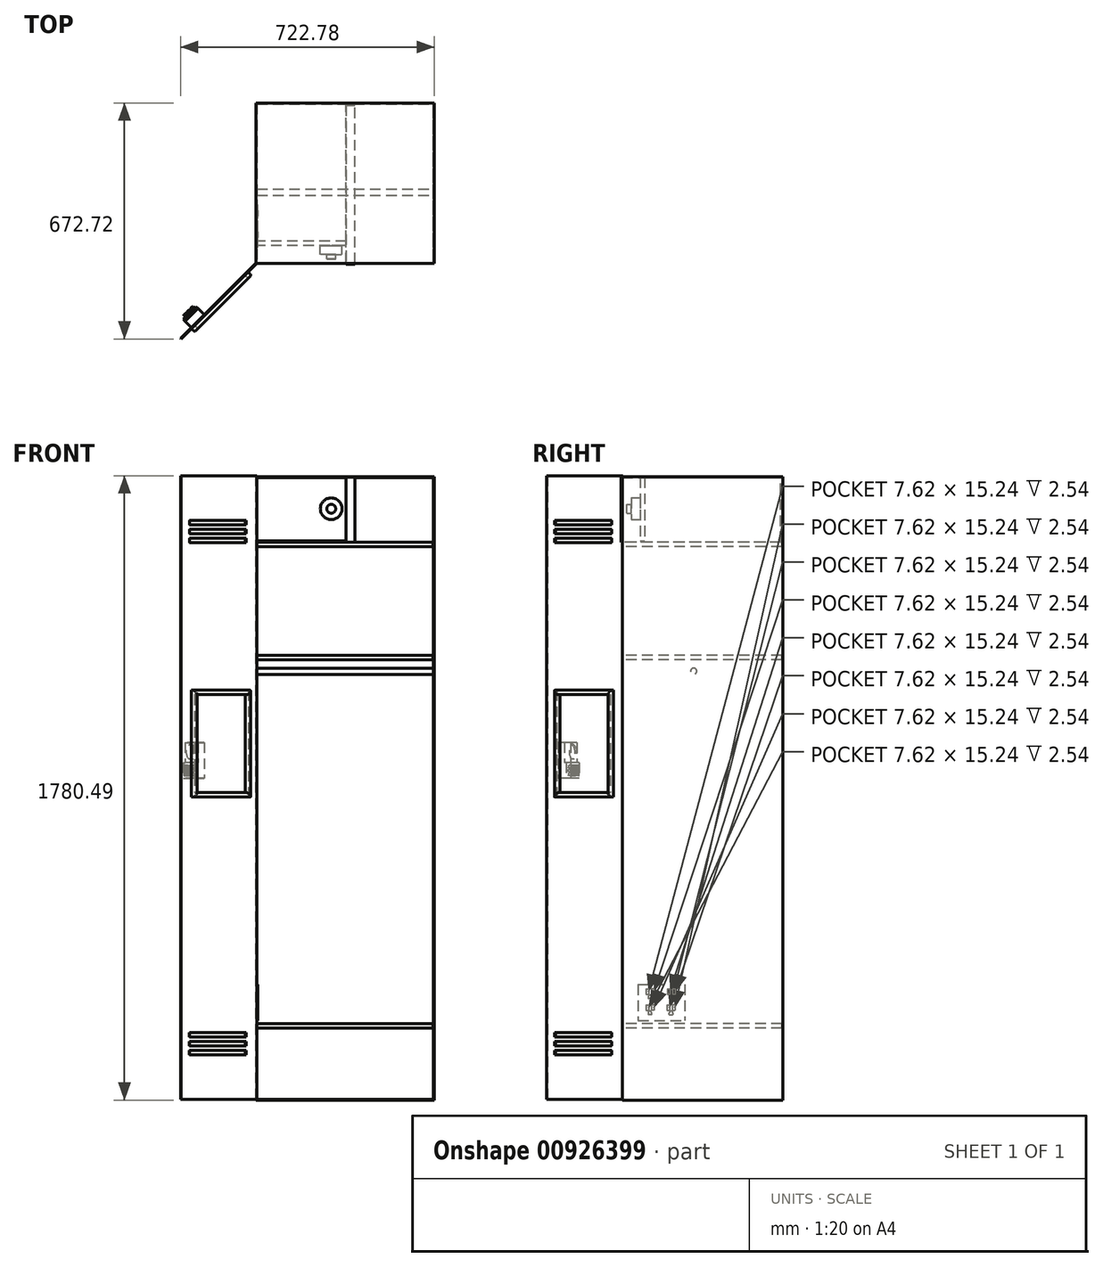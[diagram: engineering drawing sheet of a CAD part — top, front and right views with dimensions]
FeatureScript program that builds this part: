
annotation { "Feature Type Name" : "Feature", "Feature Type Description" : "" }
export const myFeature = defineFeature(function(context is Context, id is Id, definition is map)
    precondition{}
    {
        {
            var Q0;
            Q0=qCreatedBy(makeId("Front.planeOp"),FACE);
            var sketch = newSketch(context, id + "F0", { "sketchPlane" : qUnion([Q0])});
            skLineSegment(sketch, "E0.bottom", {"start": v(-28.78, 1709) * mm, "end": v(479.22, 1709) * mm});
            skLineSegment(sketch, "E0.top", {"start": v(-28.78, -69) * mm, "end": v(479.22, -69) * mm});
            skLineSegment(sketch, "E0.left", {"start": v(-28.78, 1709) * mm, "end": v(-28.78, -69) * mm});
            skLineSegment(sketch, "E0.right", {"start": v(479.22, 1709) * mm, "end": v(479.22, -69) * mm});
            skPoint(sketch, "E1", {"position": v(-28.78, 1709) * mm});
            skPoint(sketch, "E2", {"position": v(-28.78, -69) * mm});
            skSolve(sketch);
        }
        {
            var Q0;
            Q0 = qSketchRegion(id + "F0", true);
            extrude(context, id + "F1", {"entities" : qUnion([Q0]), "depth" : 457.2 * mm, "offsetDistance" : 25.4 * mm});
        }
        {
            var Q0;
            Q0=makeQuery(id+"F1.opExtrude","CAP_FACE",FACE,{"disambiguationData":[OSD([sQuery(id+"F0.wireOp",EDGE,"E0.bottom"),sQuery(id+"F0.wireOp",EDGE,"E0.top"),sQuery(id+"F0.wireOp",EDGE,"E0.left"),sQuery(id+"F0.wireOp",EDGE,"E0.right")])],"isStart":false});
            shell(context, id + "F2", {"entities" : qUnion([Q0]), "thickness" : 2.54 * mm});
        }
        {
            var Q0;
            {var subQ0=sQuery(id+"F0.wireOp",EDGE,"E0.left");Q0=makeQuery(id+"F2.opShell","OFFSET_EDGE",EDGE,{"disambiguationData":[OSD([subQ0]),TDD([makeQuery(id+"F1.opExtrude","CAP_EDGE",EDGE,{"disambiguationData":[OSD([subQ0])],"isStart":false})])]});}
            cPlane(context, id + "F3", {"entities" : qUnion([Q0]), "cplaneType" : CPlaneType.LINE_ANGLE, "offset" : 25.4 * mm, "angle" : 45 * degree, "width" : 152.4 * mm, "height" : 152.4 * mm});
        }
        {
            var Q0;
            Q0=makeQuery(id+"F2.opShell","OFFSET_FACE",FACE,{"disambiguationData":[OSD([sQuery(id+"F0.wireOp",EDGE,"E0.left")])]});
            var sketch = newSketch(context, id + "F4", { "sketchPlane" : qUnion([Q0])});
            skPoint(sketch, "E3", {"position": v(-457.2, 1706.45) * mm});
            skPoint(sketch, "E4", {"position": v(-457.2, -66.47) * mm});
            skSolve(sketch);
        }
        {
            var Q0;
            Q0=qCreatedBy(id+"F3.planeOp",FACE);
            var sketch = newSketch(context, id + "F5", { "sketchPlane" : qUnion([Q0])});
            skLineSegment(sketch, "E5.bottom", {"start": v(341.83, 1711.48) * mm, "end": v(646.63, 1711.48) * mm});
            skLineSegment(sketch, "E5.top", {"start": v(341.83, -66.52) * mm, "end": v(646.63, -66.52) * mm});
            skLineSegment(sketch, "E5.left", {"start": v(341.83, 1711.48) * mm, "end": v(341.83, -66.52) * mm});
            skLineSegment(sketch, "E5.right", {"start": v(646.63, 1711.48) * mm, "end": v(646.63, -66.52) * mm});
            skLineSegment(sketch, "E6.bottom", {"start": v(385.44, 1584.48) * mm, "end": v(614.04, 1584.48) * mm});
            skLineSegment(sketch, "E6.top", {"start": v(385.44, 1571.78) * mm, "end": v(614.04, 1571.78) * mm});
            skLineSegment(sketch, "E6.left", {"start": v(385.44, 1584.48) * mm, "end": v(385.44, 1571.78) * mm});
            skLineSegment(sketch, "E6.right", {"start": v(614.04, 1584.48) * mm, "end": v(614.04, 1571.78) * mm});
            skLineSegment(sketch, "E7.bottom", {"start": v(614.04, 1559.08) * mm, "end": v(385.44, 1559.08) * mm});
            skLineSegment(sketch, "E7.top", {"start": v(614.04, 1546.38) * mm, "end": v(385.44, 1546.38) * mm});
            skLineSegment(sketch, "E7.left", {"start": v(614.04, 1559.08) * mm, "end": v(614.04, 1546.38) * mm});
            skLineSegment(sketch, "E7.right", {"start": v(385.44, 1559.08) * mm, "end": v(385.44, 1546.38) * mm});
            skLineSegment(sketch, "E8.bottom", {"start": v(614.04, 1533.68) * mm, "end": v(385.44, 1533.68) * mm});
            skLineSegment(sketch, "E8.top", {"start": v(614.04, 1520.98) * mm, "end": v(385.44, 1520.98) * mm});
            skLineSegment(sketch, "E8.left", {"start": v(614.04, 1533.68) * mm, "end": v(614.04, 1520.98) * mm});
            skLineSegment(sketch, "E8.right", {"start": v(385.44, 1533.68) * mm, "end": v(385.44, 1520.98) * mm});
            skLineSegment(sketch, "E9", {"start": v(579.57, -66.52) * mm, "end": v(579.57, 822.48) * mm, "construction": true});
            skLineSegment(sketch, "E10", {"start": v(646.63, 822.48) * mm, "end": v(341.83, 822.48) * mm, "construction": true});
            skLineSegment(sketch, "E11.MirrorCS", {"start": v(614.04, 123.98) * mm, "end": v(385.44, 123.98) * mm});
            skLineSegment(sketch, "E12.MirrorCS", {"start": v(614.04, 111.28) * mm, "end": v(385.44, 111.28) * mm});
            skLineSegment(sketch, "E13.MirrorCS", {"start": v(614.04, 98.58) * mm, "end": v(385.44, 98.58) * mm});
            skLineSegment(sketch, "E14.MirrorCS", {"start": v(614.04, 85.88) * mm, "end": v(385.44, 85.88) * mm});
            skLineSegment(sketch, "E15.MirrorCS", {"start": v(385.44, 73.18) * mm, "end": v(614.04, 73.18) * mm});
            skLineSegment(sketch, "E16.MirrorCS", {"start": v(385.44, 60.48) * mm, "end": v(614.04, 60.48) * mm});
            skLineSegment(sketch, "E17.MirrorCS", {"start": v(385.44, 60.48) * mm, "end": v(385.44, 73.18) * mm});
            skLineSegment(sketch, "E18.MirrorCS", {"start": v(385.44, 85.88) * mm, "end": v(385.44, 98.58) * mm});
            skLineSegment(sketch, "E19.MirrorCS", {"start": v(385.44, 111.28) * mm, "end": v(385.44, 123.98) * mm});
            skLineSegment(sketch, "E20.MirrorCS", {"start": v(614.04, 111.28) * mm, "end": v(614.04, 123.98) * mm});
            skLineSegment(sketch, "E21.MirrorCS", {"start": v(614.04, 85.88) * mm, "end": v(614.04, 98.58) * mm});
            skLineSegment(sketch, "E22.MirrorCS", {"start": v(614.04, 60.48) * mm, "end": v(614.04, 73.18) * mm});
            skSolve(sketch);
        }
        {
            var Q0;
            Q0=makeQuery(id+"F5.imprint","IMPRINT",FACE,{"disambiguationData":[TD([[makeQuery(id+"F5.imprint","IMPRINT",EDGE,{"derivedFrom":sQuery(id+"F5.wireOp",EDGE,"E5.bottom")}),-1.0]])]});
            extrude(context, id + "F6", {"entities" : qUnion([Q0]), "operationType" : NewBodyOperationType.ADD, "depth" : 2.54 * mm, "offsetDistance" : 25.4 * mm});
        }
        {
            var Q0;
            Q0=makeQuery(id+"F6.opExtrude","CAP_FACE",FACE,{"disambiguationData":[OSD([sQuery(id+"F5.wireOp",EDGE,"E5.bottom"),sQuery(id+"F5.wireOp",EDGE,"E5.top"),sQuery(id+"F5.wireOp",EDGE,"E5.left"),sQuery(id+"F5.wireOp",EDGE,"E5.right"),sQuery(id+"F5.wireOp",EDGE,"E6.bottom"),sQuery(id+"F5.wireOp",EDGE,"E6.top"),sQuery(id+"F5.wireOp",EDGE,"E6.left"),sQuery(id+"F5.wireOp",EDGE,"E6.right"),sQuery(id+"F5.wireOp",EDGE,"E7.bottom"),sQuery(id+"F5.wireOp",EDGE,"E7.top"),sQuery(id+"F5.wireOp",EDGE,"E7.left"),sQuery(id+"F5.wireOp",EDGE,"E7.right"),sQuery(id+"F5.wireOp",EDGE,"E8.bottom"),sQuery(id+"F5.wireOp",EDGE,"E8.top"),sQuery(id+"F5.wireOp",EDGE,"E8.left"),sQuery(id+"F5.wireOp",EDGE,"E8.right")])],"isStart":false});
            var sketch = newSketch(context, id + "F7", { "sketchPlane" : qUnion([Q0])});
            skLineSegment(sketch, "E23.bottom", {"start": v(551.95, 950.81) * mm, "end": v(602.75, 950.81) * mm});
            skLineSegment(sketch, "E23.top", {"start": v(551.95, 849.21) * mm, "end": v(602.75, 849.21) * mm});
            skLineSegment(sketch, "E23.left", {"start": v(551.95, 950.81) * mm, "end": v(551.95, 849.21) * mm});
            skLineSegment(sketch, "E23.right", {"start": v(602.75, 950.81) * mm, "end": v(602.75, 849.21) * mm});
            skSolve(sketch);
        }
        {
            var Q0;
            Q0=makeQuery(id+"F7.imprint","IMPRINT",FACE,{"disambiguationData":[TD([[makeQuery(id+"F7.imprint","IMPRINT",EDGE,{"derivedFrom":sQuery(id+"F7.wireOp",EDGE,"E23.bottom")}),-1.0]])]});
            extrude(context, id + "F8", {"entities" : qUnion([Q0]), "operationType" : NewBodyOperationType.ADD, "depth" : 25.4 * mm, "offsetDistance" : 25.4 * mm});
        }
        {
            var Q0;
            Q0=qCreatedBy(makeId("Front.planeOp"),FACE);
            cPlane(context, id + "F9", {"entities" : qUnion([Q0]), "cplaneType" : CPlaneType.OFFSET, "offset" : 457.2 * mm, "width" : 152.4 * mm, "height" : 152.4 * mm});
        }
        {
            var Q0;
            Q0=qCreatedBy(id+"F9.planeOp",FACE);
            var sketch = newSketch(context, id + "F10", { "sketchPlane" : qUnion([Q0])});
            skLineSegment(sketch, "E24.bottom", {"start": v(-26.2, 149.43) * mm, "end": v(474.94, 149.43) * mm});
            skLineSegment(sketch, "E24.top", {"start": v(-26.2, 136.73) * mm, "end": v(474.94, 136.73) * mm});
            skLineSegment(sketch, "E24.left", {"start": v(-26.2, 149.43) * mm, "end": v(-26.2, 136.73) * mm});
            skLineSegment(sketch, "E24.right", {"start": v(474.94, 149.43) * mm, "end": v(474.94, 136.73) * mm});
            skLineSegment(sketch, "E25.bottom", {"start": v(-26.6, 1199.69) * mm, "end": v(475.38, 1199.69) * mm});
            skLineSegment(sketch, "E25.top", {"start": v(-26.6, 1186.99) * mm, "end": v(475.38, 1186.99) * mm});
            skLineSegment(sketch, "E25.left", {"start": v(-26.6, 1199.69) * mm, "end": v(-26.6, 1186.99) * mm});
            skLineSegment(sketch, "E25.right", {"start": v(475.38, 1199.69) * mm, "end": v(475.38, 1186.99) * mm});
            skLineSegment(sketch, "E26.bottom", {"start": v(-25.76, 1522.03) * mm, "end": v(475.38, 1522.03) * mm});
            skLineSegment(sketch, "E26.top", {"start": v(-25.76, 1509.33) * mm, "end": v(475.38, 1509.33) * mm});
            skLineSegment(sketch, "E26.left", {"start": v(-25.76, 1522.03) * mm, "end": v(-25.76, 1509.33) * mm});
            skLineSegment(sketch, "E26.right", {"start": v(475.38, 1522.03) * mm, "end": v(475.38, 1509.33) * mm});
            skSolve(sketch);
        }
        {
            var Q0;
            Q0=makeQuery(id+"F10.imprint","IMPRINT",FACE,{"disambiguationData":[TD([[makeQuery(id+"F10.imprint","IMPRINT",EDGE,{"derivedFrom":sQuery(id+"F10.wireOp",EDGE,"E24.bottom")}),-1.0]])]});
            var Q1;
            Q1=makeQuery(id+"F10.imprint","IMPRINT",FACE,{"disambiguationData":[TD([[makeQuery(id+"F10.imprint","IMPRINT",EDGE,{"derivedFrom":sQuery(id+"F10.wireOp",EDGE,"VyrBGK2K-1y9x-VAEc-Igx1-qJqO2NATqdDI.bottom")}),-1.0]])]});
            var Q2;
            Q2=makeQuery(id+"F10.imprint","IMPRINT",FACE,{"disambiguationData":[TD([[makeQuery(id+"F10.imprint","IMPRINT",EDGE,{"derivedFrom":sQuery(id+"F10.wireOp",EDGE,"E25.bottom")}),-1.0]])]});
            var Q3;
            Q3=makeQuery(id+"F10.imprint","IMPRINT",FACE,{"disambiguationData":[TD([[makeQuery(id+"F10.imprint","IMPRINT",EDGE,{"derivedFrom":sQuery(id+"F10.wireOp",EDGE,"E26.bottom")}),-1.0]])]});
            extrude(context, id + "F11", {"entities" : qUnion([Q0, Q1, Q2, Q3]), "operationType" : NewBodyOperationType.ADD, "endBound" : BoundingType.UP_TO_NEXT, "oppositeDirection" : true, "depth" : 25.4 * mm, "offsetDistance" : 25.4 * mm});
        }
        {
            var Q0;
            {var subQ0=sQuery(id+"F10.wireOp",EDGE,"E24.bottom");var subQ1=sQuery(id+"F0.wireOp",EDGE,"E0.right");Q0=makeQuery(id+"F11.boolean.opBoolean","SPLIT",FACE,{"disambiguationData":[TD([makeQuery(id+"F11.opExtrude","SWEPT_FACE",FACE,{"disambiguationData":[OSD([subQ0])]})])],"derivedFrom":makeQuery(id+"F2.opShell","OFFSET_FACE",FACE,{"disambiguationData":[OSD([subQ1])]})});}
            var sketch = newSketch(context, id + "F12", { "sketchPlane" : qUnion([Q0])});
            skCircle(sketch, "E27", {"center": v(253.8, 1154.02) * mm, "radius": 8.9 * mm});
            skSolve(sketch);
        }
        {
            var Q0;
            Q0=makeQuery(id+"F12.imprint","IMPRINT",FACE,{"disambiguationData":[TD([[makeQuery(id+"F12.imprint","IMPRINT",EDGE,{"derivedFrom":sQuery(id+"F12.wireOp",EDGE,"E27")}),1.0]])]});
            extrude(context, id + "F13", {"entities" : qUnion([Q0]), "operationType" : NewBodyOperationType.ADD, "endBound" : BoundingType.UP_TO_NEXT, "depth" : 25.4 * mm, "offsetDistance" : 25.4 * mm});
        }
        {
            var Q0;
            Q0=makeQuery(id+"F6.opExtrude","CAP_FACE",FACE,{"disambiguationData":[OSD([sQuery(id+"F5.wireOp",EDGE,"E5.bottom"),sQuery(id+"F5.wireOp",EDGE,"E5.top"),sQuery(id+"F5.wireOp",EDGE,"E5.left"),sQuery(id+"F5.wireOp",EDGE,"E5.right"),sQuery(id+"F5.wireOp",EDGE,"E6.bottom"),sQuery(id+"F5.wireOp",EDGE,"E6.top"),sQuery(id+"F5.wireOp",EDGE,"E6.left"),sQuery(id+"F5.wireOp",EDGE,"E6.right"),sQuery(id+"F5.wireOp",EDGE,"E7.bottom"),sQuery(id+"F5.wireOp",EDGE,"E7.top"),sQuery(id+"F5.wireOp",EDGE,"E7.left"),sQuery(id+"F5.wireOp",EDGE,"E7.right"),sQuery(id+"F5.wireOp",EDGE,"E8.bottom"),sQuery(id+"F5.wireOp",EDGE,"E8.top"),sQuery(id+"F5.wireOp",EDGE,"E8.left"),sQuery(id+"F5.wireOp",EDGE,"E8.right"),sQuery(id+"F5.wireOp",EDGE,"E11.MirrorCS"),sQuery(id+"F5.wireOp",EDGE,"E12.MirrorCS"),sQuery(id+"F5.wireOp",EDGE,"E13.MirrorCS"),sQuery(id+"F5.wireOp",EDGE,"E14.MirrorCS"),sQuery(id+"F5.wireOp",EDGE,"E15.MirrorCS"),sQuery(id+"F5.wireOp",EDGE,"E16.MirrorCS"),sQuery(id+"F5.wireOp",EDGE,"E17.MirrorCS"),sQuery(id+"F5.wireOp",EDGE,"E18.MirrorCS"),sQuery(id+"F5.wireOp",EDGE,"E19.MirrorCS"),sQuery(id+"F5.wireOp",EDGE,"E20.MirrorCS"),sQuery(id+"F5.wireOp",EDGE,"E21.MirrorCS"),sQuery(id+"F5.wireOp",EDGE,"E22.MirrorCS")])],"isStart":true});
            var sketch = newSketch(context, id + "F14", { "sketchPlane" : qUnion([Q0])});
            skLineSegment(sketch, "E28.bottom", {"start": v(-605.48, 1099.56) * mm, "end": v(-376.88, 1099.56) * mm});
            skLineSegment(sketch, "E28.top", {"start": v(-605.48, 794.76) * mm, "end": v(-376.88, 794.76) * mm});
            skLineSegment(sketch, "E28.left", {"start": v(-605.48, 1099.56) * mm, "end": v(-605.48, 794.76) * mm});
            skLineSegment(sketch, "E28.right", {"start": v(-376.88, 1099.56) * mm, "end": v(-376.88, 794.76) * mm});
            skLineSegment(sketch, "E29.0", {"start": v(-592.78, 1086.86) * mm, "end": v(-389.58, 1086.86) * mm});
            skLineSegment(sketch, "E29.1", {"start": v(-592.78, 1086.86) * mm, "end": v(-592.78, 807.46) * mm});
            skLineSegment(sketch, "E29.2", {"start": v(-592.78, 807.46) * mm, "end": v(-389.58, 807.46) * mm});
            skLineSegment(sketch, "E29.3", {"start": v(-389.58, 1086.86) * mm, "end": v(-389.58, 807.46) * mm});
            skSolve(sketch);
        }
        {
            var Q0;
            Q0=makeQuery(id+"F14.imprint","IMPRINT",FACE,{"disambiguationData":[TD([[makeQuery(id+"F14.imprint","IMPRINT",EDGE,{"derivedFrom":sQuery(id+"F14.wireOp",EDGE,"E28.bottom")}),-1.0]])]});
            extrude(context, id + "F15", {"entities" : qUnion([Q0]), "operationType" : NewBodyOperationType.ADD, "depth" : 12.7 * mm, "offsetDistance" : 25.4 * mm});
        }
        {
            var Q0;
            Q0=makeQuery(id+"F15.opExtrude","CAP_EDGE",EDGE,{"disambiguationData":[OSD([sQuery(id+"F14.wireOp",EDGE,"E28.left")])],"isStart":false});
            var Q1;
            Q1=makeQuery(id+"F15.opExtrude","CAP_EDGE",EDGE,{"disambiguationData":[OSD([sQuery(id+"F14.wireOp",EDGE,"E28.bottom")])],"isStart":false});
            var Q2;
            Q2=makeQuery(id+"F15.opExtrude","CAP_EDGE",EDGE,{"disambiguationData":[OSD([sQuery(id+"F14.wireOp",EDGE,"E28.right")])],"isStart":false});
            var Q3;
            Q3=makeQuery(id+"F15.opExtrude","CAP_EDGE",EDGE,{"disambiguationData":[OSD([sQuery(id+"F14.wireOp",EDGE,"E28.top")])],"isStart":false});
            var Q4;
            Q4=makeQuery(id+"F15.opExtrude","CAP_EDGE",EDGE,{"disambiguationData":[OSD([sQuery(id+"F14.wireOp",EDGE,"E29.2")])],"isStart":false});
            var Q5;
            Q5=makeQuery(id+"F15.opExtrude","CAP_EDGE",EDGE,{"disambiguationData":[OSD([sQuery(id+"F14.wireOp",EDGE,"E29.3")])],"isStart":false});
            var Q6;
            Q6=makeQuery(id+"F15.opExtrude","CAP_EDGE",EDGE,{"disambiguationData":[OSD([sQuery(id+"F14.wireOp",EDGE,"E29.1")])],"isStart":false});
            var Q7;
            Q7=makeQuery(id+"F15.opExtrude","CAP_EDGE",EDGE,{"disambiguationData":[OSD([sQuery(id+"F14.wireOp",EDGE,"E29.0")])],"isStart":false});
            fillet(context, id + "F16", {"entities" : qUnion([Q0, Q1, Q2, Q3, Q4, Q5, Q6, Q7]), "radius" : 5.08 * mm, "tangentPropagation" : true, "allowEdgeOverflow" : false});
        }
        {
            var Q0;
            {var subQ0=sQuery(id+"F0.wireOp",EDGE,"E0.left");Q0=makeQuery(id+"F4.imprint","IMPRINT",FACE,{"disambiguationData":[TD([[makeQuery(id+"F4.imprint","IMPRINT",EDGE,{"derivedFrom":makeQuery(id+"F2.opShell","OFFSET_EDGE",EDGE,{"disambiguationData":[OSD([subQ0]),TDD([makeQuery(id+"F1.opExtrude","CAP_EDGE",EDGE,{"disambiguationData":[OSD([subQ0])],"isStart":true})])]})}),-1.0]])]});}
            var sketch = newSketch(context, id + "F17", { "sketchPlane" : qUnion([Q0])});
            skLineSegment(sketch, "E30.bottom", {"start": v(-406.4, 1707.77) * mm, "end": v(-393.7, 1707.77) * mm});
            skLineSegment(sketch, "E30.top", {"start": v(-406.4, 1525.9) * mm, "end": v(-393.7, 1525.9) * mm});
            skLineSegment(sketch, "E30.left", {"start": v(-406.4, 1707.77) * mm, "end": v(-406.4, 1525.9) * mm});
            skLineSegment(sketch, "E30.right", {"start": v(-393.7, 1707.77) * mm, "end": v(-393.7, 1525.9) * mm});
            skSolve(sketch);
        }
        {
            var Q0;
            {var subQ0=sQuery(id+"F17.wireOp",EDGE,"E30.top");Q0=makeQuery(id+"F17.imprint","IMPRINT",FACE,{"disambiguationData":[TD([[makeQuery(id+"F17.imprint","IMPRINT",EDGE,{"derivedFrom":subQ0}),1.0]])]});}
            extrude(context, id + "F18", {"entities" : qUnion([Q0]), "operationType" : NewBodyOperationType.ADD, "depth" : 254 * mm, "offsetDistance" : 25.4 * mm});
        }
        {
            var Q0;
            Q0=makeQuery(id+"F18.opExtrude","SWEPT_FACE",FACE,{"disambiguationData":[OSD([sQuery(id+"F17.wireOp",EDGE,"E30.left")])]});
            var sketch = newSketch(context, id + "F19", { "sketchPlane" : qUnion([Q0])});
            skCircle(sketch, "E31", {"center": v(185.47, 1617.22) * mm, "radius": 31.03 * mm});
            skSolve(sketch);
        }
        {
            var Q0;
            Q0=makeQuery(id+"F19.imprint","IMPRINT",FACE,{"disambiguationData":[TD([[makeQuery(id+"F19.imprint","IMPRINT",EDGE,{"derivedFrom":sQuery(id+"F19.wireOp",EDGE,"E31")}),1.0]])]});
            extrude(context, id + "F20", {"entities" : qUnion([Q0]), "operationType" : NewBodyOperationType.ADD, "depth" : 25.4 * mm, "offsetDistance" : 25.4 * mm});
        }
        {
            var Q0;
            Q0=makeQuery(id+"F20.opExtrude","CAP_FACE",FACE,{"disambiguationData":[OSD([sQuery(id+"F19.wireOp",EDGE,"E31")])],"isStart":false});
            var sketch = newSketch(context, id + "F21", { "sketchPlane" : qUnion([Q0])});
            skCircle(sketch, "E32", {"center": v(185.47, 1617.22) * mm, "radius": 12.7 * mm});
            skSolve(sketch);
        }
        {
            var Q0;
            Q0=makeQuery(id+"F21.imprint","IMPRINT",FACE,{"disambiguationData":[TD([[makeQuery(id+"F21.imprint","IMPRINT",EDGE,{"derivedFrom":sQuery(id+"F21.wireOp",EDGE,"E32")}),1.0]])]});
            extrude(context, id + "F22", {"entities" : qUnion([Q0]), "operationType" : NewBodyOperationType.ADD, "depth" : 12.7 * mm, "offsetDistance" : 25.4 * mm});
        }
        {
            var Q0;
            Q0=makeQuery(id+"F8.opExtrude","CAP_FACE",FACE,{"disambiguationData":[OSD([sQuery(id+"F7.wireOp",EDGE,"E23.bottom"),sQuery(id+"F7.wireOp",EDGE,"E23.top"),sQuery(id+"F7.wireOp",EDGE,"E23.left"),sQuery(id+"F7.wireOp",EDGE,"E23.right")])],"isStart":false});
            var sketch = newSketch(context, id + "F23", { "sketchPlane" : qUnion([Q0])});
            skEllipse(sketch, "E33", {"center": v(576.01, 923.91) * mm, "majorRadius": 21.07 * mm, "minorRadius": 13.97 * mm, "majorAxis": v(0, 1)});
            skLineSegment(sketch, "E34.bottom", {"start": v(551.95, 893.4) * mm, "end": v(602.75, 893.4) * mm});
            skLineSegment(sketch, "E34.top", {"start": v(551.95, 849.21) * mm, "end": v(602.75, 849.21) * mm});
            skLineSegment(sketch, "E34.left", {"start": v(551.95, 893.4) * mm, "end": v(551.95, 849.21) * mm});
            skLineSegment(sketch, "E34.right", {"start": v(602.75, 893.4) * mm, "end": v(602.75, 849.21) * mm});
            skSolve(sketch);
        }
        {
            var Q0;
            Q0=makeQuery(id+"F23.imprint","IMPRINT",FACE,{"disambiguationData":[TD([[makeQuery(id+"F23.imprint","IMPRINT",EDGE,{"derivedFrom":sQuery(id+"F23.wireOp",EDGE,"E33")}),1.0]])]});
            var Q1;
            Q1=makeQuery(id+"F23.imprint","IMPRINT",FACE,{"disambiguationData":[TD([[makeQuery(id+"F23.imprint","IMPRINT",EDGE,{"derivedFrom":sQuery(id+"F23.wireOp",EDGE,"E34.bottom")}),-1.0]])]});
            extrude(context, id + "F24", {"entities" : qUnion([Q0, Q1]), "operationType" : NewBodyOperationType.ADD, "depth" : 7.62 * mm, "offsetDistance" : 25.4 * mm});
        }
        {
            var Q0;
            {var subQ0=sQuery(id+"F0.wireOp",EDGE,"E0.left");Q0=makeQuery(id+"F4.imprint","IMPRINT",FACE,{"disambiguationData":[TD([[makeQuery(id+"F4.imprint","IMPRINT",EDGE,{"derivedFrom":makeQuery(id+"F2.opShell","OFFSET_EDGE",EDGE,{"disambiguationData":[OSD([subQ0]),TDD([makeQuery(id+"F1.opExtrude","CAP_EDGE",EDGE,{"disambiguationData":[OSD([subQ0])],"isStart":true})])]})}),-1.0]])]});}
            var sketch = newSketch(context, id + "F25", { "sketchPlane" : qUnion([Q0])});
            skLineSegment(sketch, "E35.bottom", {"start": v(-411.97, 260.67) * mm, "end": v(-278.8, 260.67) * mm});
            skLineSegment(sketch, "E35.top", {"start": v(-411.97, 157.65) * mm, "end": v(-278.8, 157.65) * mm});
            skLineSegment(sketch, "E35.left", {"start": v(-411.97, 260.67) * mm, "end": v(-411.97, 157.65) * mm});
            skLineSegment(sketch, "E35.right", {"start": v(-278.8, 260.67) * mm, "end": v(-278.8, 157.65) * mm});
            skSolve(sketch);
        }
        {
            var Q0;
            Q0=makeQuery(id+"F25.imprint","IMPRINT",FACE,{"disambiguationData":[TD([[makeQuery(id+"F25.imprint","IMPRINT",EDGE,{"derivedFrom":sQuery(id+"F25.wireOp",EDGE,"E35.bottom")}),-1.0]])]});
            extrude(context, id + "F26", {"entities" : qUnion([Q0]), "operationType" : NewBodyOperationType.ADD, "depth" : 2.54 * mm, "offsetDistance" : 25.4 * mm});
        }
        {
            var Q0;
            Q0=makeQuery(id+"F24.opExtrude","CAP_FACE",FACE,{"disambiguationData":[OSD([sQuery(id+"F23.wireOp",EDGE,"E34.bottom"),sQuery(id+"F23.wireOp",EDGE,"E34.top"),sQuery(id+"F23.wireOp",EDGE,"E34.left"),sQuery(id+"F23.wireOp",EDGE,"E34.right")])],"isStart":false});
            var sketch = newSketch(context, id + "F27", { "sketchPlane" : qUnion([Q0])});
            skLineSegment(sketch, "E36.bottom", {"start": v(558.7, 885.35) * mm, "end": v(566.16, 885.35) * mm});
            skLineSegment(sketch, "E36.top", {"start": v(558.7, 877.89) * mm, "end": v(566.16, 877.89) * mm});
            skLineSegment(sketch, "E36.left", {"start": v(558.7, 885.35) * mm, "end": v(558.7, 877.89) * mm});
            skLineSegment(sketch, "E36.right", {"start": v(566.16, 885.35) * mm, "end": v(566.16, 877.89) * mm});
            skLineSegment(sketch, "E37", {"start": v(569.23, 890.17) * mm, "end": v(569.23, 876.13) * mm, "construction": true});
            skLineSegment(sketch, "E38.MirrorCS", {"start": v(579.77, 877.89) * mm, "end": v(572.3, 877.89) * mm});
            skLineSegment(sketch, "E39.MirrorCS", {"start": v(572.3, 885.35) * mm, "end": v(572.3, 877.89) * mm});
            skLineSegment(sketch, "E40.MirrorCS", {"start": v(579.77, 885.35) * mm, "end": v(572.3, 885.35) * mm});
            skLineSegment(sketch, "E41.MirrorCS", {"start": v(579.77, 885.35) * mm, "end": v(579.77, 877.89) * mm});
            skLineSegment(sketch, "E42", {"start": v(583.06, 886.66) * mm, "end": v(583.06, 854.85) * mm, "construction": true});
            skLineSegment(sketch, "E43.MirrorCS", {"start": v(586.35, 885.35) * mm, "end": v(593.8, 885.35) * mm});
            skLineSegment(sketch, "E44.MirrorCS", {"start": v(586.35, 885.35) * mm, "end": v(586.35, 877.89) * mm});
            skLineSegment(sketch, "E45.MirrorCS", {"start": v(586.35, 877.89) * mm, "end": v(593.8, 877.89) * mm});
            skLineSegment(sketch, "E46.MirrorCS", {"start": v(593.8, 885.35) * mm, "end": v(593.8, 877.89) * mm});
            skLineSegment(sketch, "E47", {"start": v(569.23, 876.13) * mm, "end": v(556.5, 876.13) * mm, "construction": true});
            skLineSegment(sketch, "E48.MirrorCS", {"start": v(558.7, 874.38) * mm, "end": v(566.16, 874.38) * mm});
            skLineSegment(sketch, "E49.MirrorCS", {"start": v(566.16, 866.92) * mm, "end": v(566.16, 874.38) * mm});
            skLineSegment(sketch, "E50.MirrorCS", {"start": v(558.7, 866.92) * mm, "end": v(566.16, 866.92) * mm});
            skLineSegment(sketch, "E51.MirrorCS", {"start": v(558.7, 866.92) * mm, "end": v(558.7, 874.38) * mm});
            skLineSegment(sketch, "E52.MirrorCS", {"start": v(569.23, 862.09) * mm, "end": v(569.23, 876.13) * mm, "construction": true});
            skLineSegment(sketch, "E53.MirrorCS", {"start": v(579.77, 866.92) * mm, "end": v(572.3, 866.92) * mm});
            skLineSegment(sketch, "E54.MirrorCS", {"start": v(579.77, 866.92) * mm, "end": v(579.77, 874.38) * mm});
            skLineSegment(sketch, "E55.MirrorCS", {"start": v(572.3, 866.92) * mm, "end": v(572.3, 874.38) * mm});
            skLineSegment(sketch, "E56.MirrorCS", {"start": v(579.77, 874.38) * mm, "end": v(572.3, 874.38) * mm});
            skLineSegment(sketch, "E57.MirrorCS", {"start": v(586.35, 866.92) * mm, "end": v(586.35, 874.38) * mm});
            skLineSegment(sketch, "E58.MirrorCS", {"start": v(586.35, 874.38) * mm, "end": v(593.8, 874.38) * mm});
            skLineSegment(sketch, "E59.MirrorCS", {"start": v(593.8, 866.92) * mm, "end": v(593.8, 874.38) * mm});
            skLineSegment(sketch, "E60.MirrorCS", {"start": v(586.35, 866.92) * mm, "end": v(593.8, 866.92) * mm});
            skLineSegment(sketch, "E61", {"start": v(569.23, 865.16) * mm, "end": v(556.29, 865.16) * mm, "construction": true});
            skLineSegment(sketch, "E62.MirrorCS", {"start": v(558.7, 863.4) * mm, "end": v(558.7, 855.94) * mm});
            skLineSegment(sketch, "E63.MirrorCS", {"start": v(558.7, 855.94) * mm, "end": v(566.16, 855.94) * mm});
            skLineSegment(sketch, "E64.MirrorCS", {"start": v(566.16, 863.4) * mm, "end": v(566.16, 855.94) * mm});
            skLineSegment(sketch, "E65.MirrorCS", {"start": v(558.7, 863.4) * mm, "end": v(566.16, 863.4) * mm});
            skLineSegment(sketch, "E66.MirrorCS", {"start": v(579.77, 855.94) * mm, "end": v(572.3, 855.94) * mm});
            skLineSegment(sketch, "E67.MirrorCS", {"start": v(579.77, 863.4) * mm, "end": v(579.77, 855.94) * mm});
            skLineSegment(sketch, "E68.MirrorCS", {"start": v(572.3, 863.4) * mm, "end": v(572.3, 855.94) * mm});
            skLineSegment(sketch, "E69.MirrorCS", {"start": v(579.77, 863.4) * mm, "end": v(572.3, 863.4) * mm});
            skLineSegment(sketch, "E70.MirrorCS", {"start": v(593.8, 863.4) * mm, "end": v(593.8, 855.94) * mm});
            skLineSegment(sketch, "E71.MirrorCS", {"start": v(586.35, 855.94) * mm, "end": v(593.8, 855.94) * mm});
            skLineSegment(sketch, "E72.MirrorCS", {"start": v(586.35, 863.4) * mm, "end": v(593.8, 863.4) * mm});
            skLineSegment(sketch, "E73.MirrorCS", {"start": v(586.35, 863.4) * mm, "end": v(586.35, 855.94) * mm});
            skSolve(sketch);
        }
        {
            var Q0;
            Q0 = qSketchRegion(id + "F27", true);
            extrude(context, id + "F28", {"entities" : qUnion([Q0]), "operationType" : NewBodyOperationType.ADD, "depth" : 7.62 * mm, "offsetDistance" : 25.4 * mm});
        }
        {
            var Q0;
            Q0=makeQuery(id+"F28.opExtrude","CAP_FACE",FACE,{"disambiguationData":[OSD([sQuery(id+"F27.wireOp",EDGE,"E36.bottom"),sQuery(id+"F27.wireOp",EDGE,"E36.top"),sQuery(id+"F27.wireOp",EDGE,"E36.left"),sQuery(id+"F27.wireOp",EDGE,"E36.right")])],"isStart":false});
            var Q1;
            Q1=makeQuery(id+"F28.opExtrude","CAP_FACE",FACE,{"disambiguationData":[OSD([sQuery(id+"F27.wireOp",EDGE,"E38.MirrorCS"),sQuery(id+"F27.wireOp",EDGE,"E39.MirrorCS"),sQuery(id+"F27.wireOp",EDGE,"E40.MirrorCS"),sQuery(id+"F27.wireOp",EDGE,"E41.MirrorCS")])],"isStart":false});
            var Q2;
            Q2=makeQuery(id+"F28.opExtrude","CAP_FACE",FACE,{"disambiguationData":[OSD([sQuery(id+"F27.wireOp",EDGE,"E43.MirrorCS"),sQuery(id+"F27.wireOp",EDGE,"E44.MirrorCS"),sQuery(id+"F27.wireOp",EDGE,"E45.MirrorCS"),sQuery(id+"F27.wireOp",EDGE,"E46.MirrorCS")])],"isStart":false});
            var Q3;
            Q3=makeQuery(id+"F28.opExtrude","CAP_FACE",FACE,{"disambiguationData":[OSD([sQuery(id+"F27.wireOp",EDGE,"E57.MirrorCS"),sQuery(id+"F27.wireOp",EDGE,"E58.MirrorCS"),sQuery(id+"F27.wireOp",EDGE,"E59.MirrorCS"),sQuery(id+"F27.wireOp",EDGE,"E60.MirrorCS")])],"isStart":false});
            var Q4;
            Q4=makeQuery(id+"F28.opExtrude","CAP_FACE",FACE,{"disambiguationData":[OSD([sQuery(id+"F27.wireOp",EDGE,"E53.MirrorCS"),sQuery(id+"F27.wireOp",EDGE,"E54.MirrorCS"),sQuery(id+"F27.wireOp",EDGE,"E55.MirrorCS"),sQuery(id+"F27.wireOp",EDGE,"E56.MirrorCS")])],"isStart":false});
            var Q5;
            Q5=makeQuery(id+"F28.opExtrude","CAP_FACE",FACE,{"disambiguationData":[OSD([sQuery(id+"F27.wireOp",EDGE,"E48.MirrorCS"),sQuery(id+"F27.wireOp",EDGE,"E49.MirrorCS"),sQuery(id+"F27.wireOp",EDGE,"E50.MirrorCS"),sQuery(id+"F27.wireOp",EDGE,"E51.MirrorCS")])],"isStart":false});
            var Q6;
            Q6=makeQuery(id+"F28.opExtrude","CAP_FACE",FACE,{"disambiguationData":[OSD([sQuery(id+"F27.wireOp",EDGE,"E62.MirrorCS"),sQuery(id+"F27.wireOp",EDGE,"E63.MirrorCS"),sQuery(id+"F27.wireOp",EDGE,"E64.MirrorCS"),sQuery(id+"F27.wireOp",EDGE,"E65.MirrorCS")])],"isStart":false});
            var Q7;
            Q7=makeQuery(id+"F28.opExtrude","CAP_FACE",FACE,{"disambiguationData":[OSD([sQuery(id+"F27.wireOp",EDGE,"E66.MirrorCS"),sQuery(id+"F27.wireOp",EDGE,"E67.MirrorCS"),sQuery(id+"F27.wireOp",EDGE,"E68.MirrorCS"),sQuery(id+"F27.wireOp",EDGE,"E69.MirrorCS")])],"isStart":false});
            var Q8;
            Q8=makeQuery(id+"F28.opExtrude","CAP_FACE",FACE,{"disambiguationData":[OSD([sQuery(id+"F27.wireOp",EDGE,"E70.MirrorCS"),sQuery(id+"F27.wireOp",EDGE,"E71.MirrorCS"),sQuery(id+"F27.wireOp",EDGE,"E72.MirrorCS"),sQuery(id+"F27.wireOp",EDGE,"E73.MirrorCS")])],"isStart":false});
            var Q9;
            Q9=makeQuery(id+"F28.opExtrude","SWEPT_EDGE",EDGE,{"disambiguationData":[OSD([sQuery(id+"F27.wireOp",EDGE,"E62.MirrorCS"),sQuery(id+"F27.wireOp",EDGE,"E63.MirrorCS")])]});
            var Q10;
            Q10=makeQuery(id+"F28.opExtrude","SWEPT_EDGE",EDGE,{"disambiguationData":[OSD([sQuery(id+"F27.wireOp",EDGE,"E62.MirrorCS"),sQuery(id+"F27.wireOp",EDGE,"E65.MirrorCS")])]});
            var Q11;
            Q11=makeQuery(id+"F28.opExtrude","SWEPT_EDGE",EDGE,{"disambiguationData":[OSD([sQuery(id+"F27.wireOp",EDGE,"E63.MirrorCS"),sQuery(id+"F27.wireOp",EDGE,"E64.MirrorCS")])]});
            var Q12;
            Q12=makeQuery(id+"F28.opExtrude","SWEPT_EDGE",EDGE,{"disambiguationData":[OSD([sQuery(id+"F27.wireOp",EDGE,"E66.MirrorCS"),sQuery(id+"F27.wireOp",EDGE,"E68.MirrorCS")])]});
            var Q13;
            Q13=makeQuery(id+"F28.opExtrude","SWEPT_EDGE",EDGE,{"disambiguationData":[OSD([sQuery(id+"F27.wireOp",EDGE,"E68.MirrorCS"),sQuery(id+"F27.wireOp",EDGE,"E69.MirrorCS")])]});
            var Q14;
            Q14=makeQuery(id+"F28.opExtrude","SWEPT_EDGE",EDGE,{"disambiguationData":[OSD([sQuery(id+"F27.wireOp",EDGE,"E53.MirrorCS"),sQuery(id+"F27.wireOp",EDGE,"E55.MirrorCS")])]});
            var Q15;
            Q15=makeQuery(id+"F28.opExtrude","SWEPT_EDGE",EDGE,{"disambiguationData":[OSD([sQuery(id+"F27.wireOp",EDGE,"E55.MirrorCS"),sQuery(id+"F27.wireOp",EDGE,"E56.MirrorCS")])]});
            var Q16;
            Q16=makeQuery(id+"F28.opExtrude","SWEPT_EDGE",EDGE,{"disambiguationData":[OSD([sQuery(id+"F27.wireOp",EDGE,"E38.MirrorCS"),sQuery(id+"F27.wireOp",EDGE,"E39.MirrorCS")])]});
            var Q17;
            Q17=makeQuery(id+"F28.opExtrude","SWEPT_EDGE",EDGE,{"disambiguationData":[OSD([sQuery(id+"F27.wireOp",EDGE,"E39.MirrorCS"),sQuery(id+"F27.wireOp",EDGE,"E40.MirrorCS")])]});
            var Q18;
            Q18=makeQuery(id+"F28.opExtrude","SWEPT_EDGE",EDGE,{"disambiguationData":[OSD([sQuery(id+"F27.wireOp",EDGE,"E50.MirrorCS"),sQuery(id+"F27.wireOp",EDGE,"E51.MirrorCS")])]});
            var Q19;
            Q19=makeQuery(id+"F28.opExtrude","SWEPT_EDGE",EDGE,{"disambiguationData":[OSD([sQuery(id+"F27.wireOp",EDGE,"E48.MirrorCS"),sQuery(id+"F27.wireOp",EDGE,"E51.MirrorCS")])]});
            var Q20;
            Q20=makeQuery(id+"F28.opExtrude","SWEPT_EDGE",EDGE,{"disambiguationData":[OSD([sQuery(id+"F27.wireOp",EDGE,"E36.top"),sQuery(id+"F27.wireOp",EDGE,"E36.left")])]});
            var Q21;
            Q21=makeQuery(id+"F28.opExtrude","SWEPT_EDGE",EDGE,{"disambiguationData":[OSD([sQuery(id+"F27.wireOp",EDGE,"E36.bottom"),sQuery(id+"F27.wireOp",EDGE,"E36.left")])]});
            var Q22;
            Q22=makeQuery(id+"F28.opExtrude","SWEPT_EDGE",EDGE,{"disambiguationData":[OSD([sQuery(id+"F27.wireOp",EDGE,"E38.MirrorCS"),sQuery(id+"F27.wireOp",EDGE,"E41.MirrorCS")])]});
            var Q23;
            Q23=makeQuery(id+"F28.opExtrude","SWEPT_EDGE",EDGE,{"disambiguationData":[OSD([sQuery(id+"F27.wireOp",EDGE,"E53.MirrorCS"),sQuery(id+"F27.wireOp",EDGE,"E54.MirrorCS")])]});
            var Q24;
            Q24=makeQuery(id+"F28.opExtrude","SWEPT_EDGE",EDGE,{"disambiguationData":[OSD([sQuery(id+"F27.wireOp",EDGE,"E49.MirrorCS"),sQuery(id+"F27.wireOp",EDGE,"E50.MirrorCS")])]});
            var Q25;
            Q25=makeQuery(id+"F28.opExtrude","SWEPT_EDGE",EDGE,{"disambiguationData":[OSD([sQuery(id+"F27.wireOp",EDGE,"E66.MirrorCS"),sQuery(id+"F27.wireOp",EDGE,"E67.MirrorCS")])]});
            var Q26;
            Q26=makeQuery(id+"F28.opExtrude","SWEPT_EDGE",EDGE,{"disambiguationData":[OSD([sQuery(id+"F27.wireOp",EDGE,"E71.MirrorCS"),sQuery(id+"F27.wireOp",EDGE,"E73.MirrorCS")])]});
            var Q27;
            Q27=makeQuery(id+"F28.opExtrude","SWEPT_EDGE",EDGE,{"disambiguationData":[OSD([sQuery(id+"F27.wireOp",EDGE,"E72.MirrorCS"),sQuery(id+"F27.wireOp",EDGE,"E73.MirrorCS")])]});
            var Q28;
            Q28=makeQuery(id+"F28.opExtrude","SWEPT_EDGE",EDGE,{"disambiguationData":[OSD([sQuery(id+"F27.wireOp",EDGE,"E57.MirrorCS"),sQuery(id+"F27.wireOp",EDGE,"E60.MirrorCS")])]});
            var Q29;
            Q29=makeQuery(id+"F28.opExtrude","SWEPT_EDGE",EDGE,{"disambiguationData":[OSD([sQuery(id+"F27.wireOp",EDGE,"E57.MirrorCS"),sQuery(id+"F27.wireOp",EDGE,"E58.MirrorCS")])]});
            var Q30;
            Q30=makeQuery(id+"F28.opExtrude","SWEPT_EDGE",EDGE,{"disambiguationData":[OSD([sQuery(id+"F27.wireOp",EDGE,"E44.MirrorCS"),sQuery(id+"F27.wireOp",EDGE,"E45.MirrorCS")])]});
            var Q31;
            Q31=makeQuery(id+"F28.opExtrude","SWEPT_EDGE",EDGE,{"disambiguationData":[OSD([sQuery(id+"F27.wireOp",EDGE,"E43.MirrorCS"),sQuery(id+"F27.wireOp",EDGE,"E44.MirrorCS")])]});
            var Q32;
            Q32=makeQuery(id+"F28.opExtrude","SWEPT_EDGE",EDGE,{"disambiguationData":[OSD([sQuery(id+"F27.wireOp",EDGE,"E70.MirrorCS"),sQuery(id+"F27.wireOp",EDGE,"E71.MirrorCS")])]});
            var Q33;
            Q33=makeQuery(id+"F28.opExtrude","SWEPT_EDGE",EDGE,{"disambiguationData":[OSD([sQuery(id+"F27.wireOp",EDGE,"E59.MirrorCS"),sQuery(id+"F27.wireOp",EDGE,"E60.MirrorCS")])]});
            var Q34;
            Q34=makeQuery(id+"F28.opExtrude","SWEPT_EDGE",EDGE,{"disambiguationData":[OSD([sQuery(id+"F27.wireOp",EDGE,"E45.MirrorCS"),sQuery(id+"F27.wireOp",EDGE,"E46.MirrorCS")])]});
            var Q35;
            Q35=makeQuery(id+"F28.opExtrude","SWEPT_EDGE",EDGE,{"disambiguationData":[OSD([sQuery(id+"F27.wireOp",EDGE,"E43.MirrorCS"),sQuery(id+"F27.wireOp",EDGE,"E46.MirrorCS")])]});
            var Q36;
            Q36=makeQuery(id+"F28.opExtrude","SWEPT_EDGE",EDGE,{"disambiguationData":[OSD([sQuery(id+"F27.wireOp",EDGE,"E58.MirrorCS"),sQuery(id+"F27.wireOp",EDGE,"E59.MirrorCS")])]});
            var Q37;
            Q37=makeQuery(id+"F28.opExtrude","SWEPT_EDGE",EDGE,{"disambiguationData":[OSD([sQuery(id+"F27.wireOp",EDGE,"E70.MirrorCS"),sQuery(id+"F27.wireOp",EDGE,"E72.MirrorCS")])]});
            var Q38;
            Q38=makeQuery(id+"F28.opExtrude","SWEPT_EDGE",EDGE,{"disambiguationData":[OSD([sQuery(id+"F27.wireOp",EDGE,"E67.MirrorCS"),sQuery(id+"F27.wireOp",EDGE,"E69.MirrorCS")])]});
            var Q39;
            Q39=makeQuery(id+"F28.opExtrude","SWEPT_EDGE",EDGE,{"disambiguationData":[OSD([sQuery(id+"F27.wireOp",EDGE,"E54.MirrorCS"),sQuery(id+"F27.wireOp",EDGE,"E56.MirrorCS")])]});
            var Q40;
            Q40=makeQuery(id+"F28.opExtrude","SWEPT_EDGE",EDGE,{"disambiguationData":[OSD([sQuery(id+"F27.wireOp",EDGE,"E40.MirrorCS"),sQuery(id+"F27.wireOp",EDGE,"E41.MirrorCS")])]});
            var Q41;
            Q41=makeQuery(id+"F28.opExtrude","SWEPT_EDGE",EDGE,{"disambiguationData":[OSD([sQuery(id+"F27.wireOp",EDGE,"E36.bottom"),sQuery(id+"F27.wireOp",EDGE,"E36.right")])]});
            var Q42;
            Q42=makeQuery(id+"F28.opExtrude","SWEPT_EDGE",EDGE,{"disambiguationData":[OSD([sQuery(id+"F27.wireOp",EDGE,"E48.MirrorCS"),sQuery(id+"F27.wireOp",EDGE,"E49.MirrorCS")])]});
            var Q43;
            Q43=makeQuery(id+"F28.opExtrude","SWEPT_EDGE",EDGE,{"disambiguationData":[OSD([sQuery(id+"F27.wireOp",EDGE,"E64.MirrorCS"),sQuery(id+"F27.wireOp",EDGE,"E65.MirrorCS")])]});
            fillet(context, id + "F29", {"entities" : qUnion([Q0, Q1, Q2, Q3, Q4, Q5, Q6, Q7, Q8, Q9, Q10, Q11, Q12, Q13, Q14, Q15, Q16, Q17, Q18, Q19, Q20, Q21, Q22, Q23, Q24, Q25, Q26, Q27, Q28, Q29, Q30, Q31, Q32, Q33, Q34, Q35, Q36, Q37, Q38, Q39, Q40, Q41, Q42, Q43]), "radius" : 1.27 * mm, "tangentPropagation" : true, "allowEdgeOverflow" : false});
        }
        {
            var Q0;
            Q0=makeQuery(id+"F18.opExtrude","CAP_FACE",FACE,{"disambiguationData":[OSD([sQuery(id+"F0.wireOp",EDGE,"E0.bottom"),sQuery(id+"F0.wireOp",EDGE,"E0.left"),sQuery(id+"F17.wireOp",EDGE,"E30.top"),sQuery(id+"F17.wireOp",EDGE,"E30.left"),sQuery(id+"F17.wireOp",EDGE,"E30.right")])],"isStart":false});
            var sketch = newSketch(context, id + "F30", { "sketchPlane" : qUnion([Q0])});
            skLineSegment(sketch, "E74.bottom", {"start": v(-460.19, 1521.77) * mm, "end": v(-6.52, 1521.77) * mm});
            skLineSegment(sketch, "E74.top", {"start": v(-460.19, 1706.78) * mm, "end": v(-6.52, 1706.78) * mm});
            skLineSegment(sketch, "E74.left", {"start": v(-460.19, 1521.77) * mm, "end": v(-460.19, 1706.78) * mm});
            skLineSegment(sketch, "E74.right", {"start": v(-6.52, 1521.77) * mm, "end": v(-6.52, 1706.78) * mm});
            skSolve(sketch);
        }
        {
            var Q0;
            Q0 = qSketchRegion(id + "F30", true);
            extrude(context, id + "F31", {"entities" : qUnion([Q0]), "operationType" : NewBodyOperationType.ADD, "depth" : 25.4 * mm, "offsetDistance" : 25.4 * mm});
        }
        {
            var Q0;
            Q0=makeQuery(id+"F26.opExtrude","CAP_FACE",FACE,{"disambiguationData":[OSD([sQuery(id+"F25.wireOp",EDGE,"E35.bottom"),sQuery(id+"F25.wireOp",EDGE,"E35.top"),sQuery(id+"F25.wireOp",EDGE,"E35.left"),sQuery(id+"F25.wireOp",EDGE,"E35.right")])],"isStart":false});
            var sketch = newSketch(context, id + "F32", { "sketchPlane" : qUnion([Q0])});
            skLineSegment(sketch, "E75.bottom", {"start": v(-389.98, 247.56) * mm, "end": v(-382.36, 247.56) * mm});
            skLineSegment(sketch, "E75.top", {"start": v(-389.98, 232.32) * mm, "end": v(-382.36, 232.32) * mm});
            skLineSegment(sketch, "E75.left", {"start": v(-389.98, 247.56) * mm, "end": v(-389.98, 232.32) * mm});
            skLineSegment(sketch, "E75.right", {"start": v(-382.36, 247.56) * mm, "end": v(-382.36, 232.32) * mm});
            skLineSegment(sketch, "E76", {"start": v(-382.36, 239.94) * mm, "end": v(-374.74, 239.94) * mm, "construction": true});
            skLineSegment(sketch, "E77", {"start": v(-378.55, 232.31) * mm, "end": v(-378.55, 239.94) * mm, "construction": true});
            skLineSegment(sketch, "E78.MirrorCS", {"start": v(-374.74, 247.56) * mm, "end": v(-374.74, 232.32) * mm});
            skLineSegment(sketch, "E79.MirrorCS", {"start": v(-367.12, 247.56) * mm, "end": v(-374.74, 247.56) * mm});
            skLineSegment(sketch, "E80.MirrorCS", {"start": v(-367.12, 247.56) * mm, "end": v(-367.12, 232.32) * mm});
            skLineSegment(sketch, "E81.MirrorCS", {"start": v(-367.12, 232.32) * mm, "end": v(-374.74, 232.32) * mm});
            skLineSegment(sketch, "E82", {"start": v(-378.55, 239.94) * mm, "end": v(-378.55, 224.7) * mm, "construction": true});
            skArc(sketch, "E83", {"start": v(-383.63, 224.7) * mm, "mid": v(-378.55, 229.78) * mm, "end": v(-373.47, 224.7) * mm});
            skLineSegment(sketch, "E84", {"start": v(-383.63, 224.7) * mm, "end": v(-383.63, 219.76) * mm});
            skLineSegment(sketch, "E85", {"start": v(-373.47, 219.76) * mm, "end": v(-373.47, 224.7) * mm});
            skLineSegment(sketch, "E86", {"start": v(-373.47, 219.76) * mm, "end": v(-383.63, 219.76) * mm});
            skLineSegment(sketch, "E87", {"start": v(-367.12, 232.32) * mm, "end": v(-348.07, 232.32) * mm, "construction": true});
            skLineSegment(sketch, "E88", {"start": v(-348.07, 215.1) * mm, "end": v(-348.07, 249.55) * mm, "construction": true});
            skLineSegment(sketch, "E89.MirrorCS", {"start": v(-329.02, 232.32) * mm, "end": v(-321.4, 232.32) * mm});
            skLineSegment(sketch, "E90.MirrorCS", {"start": v(-329.02, 247.56) * mm, "end": v(-329.02, 232.32) * mm});
            skLineSegment(sketch, "E91.MirrorCS", {"start": v(-329.02, 247.56) * mm, "end": v(-321.4, 247.56) * mm});
            skLineSegment(sketch, "E92.MirrorCS", {"start": v(-321.4, 247.56) * mm, "end": v(-321.4, 232.32) * mm});
            skLineSegment(sketch, "E93.MirrorCS", {"start": v(-313.78, 247.56) * mm, "end": v(-313.78, 232.32) * mm});
            skLineSegment(sketch, "E94.MirrorCS", {"start": v(-306.16, 247.56) * mm, "end": v(-313.78, 247.56) * mm});
            skLineSegment(sketch, "E95.MirrorCS", {"start": v(-306.16, 247.56) * mm, "end": v(-306.16, 232.32) * mm});
            skLineSegment(sketch, "E96.MirrorCS", {"start": v(-322.67, 219.76) * mm, "end": v(-312.5, 219.76) * mm});
            skLineSegment(sketch, "E97.MirrorCS", {"start": v(-322.67, 219.76) * mm, "end": v(-322.67, 224.7) * mm});
            skLineSegment(sketch, "E98.MirrorCS", {"start": v(-312.5, 224.7) * mm, "end": v(-312.5, 219.76) * mm});
            skArc(sketch, "E99.MirrorCS", {"start": v(-312.5, 224.7) * mm, "mid": v(-317.59, 229.78) * mm, "end": v(-322.67, 224.7) * mm});
            skLineSegment(sketch, "E100.MirrorCS", {"start": v(-306.16, 232.32) * mm, "end": v(-313.78, 232.32) * mm});
            skLineSegment(sketch, "E101", {"start": v(-378.55, 219.76) * mm, "end": v(-378.55, 201.98) * mm, "construction": true});
            skLineSegment(sketch, "E102", {"start": v(-374.57, 201.98) * mm, "end": v(-382.53, 201.98) * mm, "construction": true});
            skLineSegment(sketch, "E103.1.0.0", {"start": v(-390.22, 202.1) * mm, "end": v(-390.22, 186.86) * mm});
            skLineSegment(sketch, "E103.1.0.1", {"start": v(-390.22, 202.1) * mm, "end": v(-382.6, 202.1) * mm});
            skLineSegment(sketch, "E103.1.0.2", {"start": v(-382.6, 202.1) * mm, "end": v(-382.6, 186.86) * mm});
            skLineSegment(sketch, "E103.1.0.3", {"start": v(-390.22, 186.86) * mm, "end": v(-382.6, 186.86) * mm});
            skArc(sketch, "E103.1.0.4", {"start": v(-383.87, 179.24) * mm, "mid": v(-378.79, 184.32) * mm, "end": v(-373.7, 179.24) * mm});
            skLineSegment(sketch, "E103.1.0.5", {"start": v(-383.87, 179.24) * mm, "end": v(-383.87, 174.3) * mm});
            skLineSegment(sketch, "E103.1.0.6", {"start": v(-373.7, 174.3) * mm, "end": v(-383.87, 174.3) * mm});
            skLineSegment(sketch, "E103.1.0.7", {"start": v(-373.7, 174.3) * mm, "end": v(-373.7, 179.24) * mm});
            skLineSegment(sketch, "E103.1.0.8", {"start": v(-367.36, 186.86) * mm, "end": v(-374.98, 186.86) * mm});
            skLineSegment(sketch, "E103.1.0.9", {"start": v(-374.98, 202.1) * mm, "end": v(-374.98, 186.86) * mm});
            skLineSegment(sketch, "E103.1.0.10", {"start": v(-367.36, 202.1) * mm, "end": v(-374.98, 202.1) * mm});
            skLineSegment(sketch, "E103.1.0.11", {"start": v(-367.36, 202.1) * mm, "end": v(-367.36, 186.86) * mm});
            skLineSegment(sketch, "E103.direction1", {"start": v(-389.98, 232.32) * mm, "end": v(-390.22, 186.86) * mm, "construction": true});
            skLineSegment(sketch, "E104.1.0.0", {"start": v(-329.43, 202.1) * mm, "end": v(-329.43, 186.86) * mm});
            skLineSegment(sketch, "E104.1.0.1", {"start": v(-329.43, 186.86) * mm, "end": v(-321.8, 186.86) * mm});
            skLineSegment(sketch, "E104.1.0.2", {"start": v(-321.8, 202.1) * mm, "end": v(-321.8, 186.86) * mm});
            skLineSegment(sketch, "E104.1.0.3", {"start": v(-329.43, 202.1) * mm, "end": v(-321.8, 202.1) * mm});
            skLineSegment(sketch, "E104.1.0.4", {"start": v(-314.19, 202.1) * mm, "end": v(-314.19, 186.86) * mm});
            skLineSegment(sketch, "E104.1.0.5", {"start": v(-306.57, 202.1) * mm, "end": v(-314.19, 202.1) * mm});
            skLineSegment(sketch, "E104.1.0.6", {"start": v(-306.57, 202.1) * mm, "end": v(-306.57, 186.86) * mm});
            skArc(sketch, "E104.1.0.7", {"start": v(-312.92, 179.24) * mm, "mid": v(-318, 184.32) * mm, "end": v(-323.08, 179.24) * mm});
            skLineSegment(sketch, "E104.1.0.8", {"start": v(-312.92, 179.24) * mm, "end": v(-312.92, 174.3) * mm});
            skLineSegment(sketch, "E104.1.0.9", {"start": v(-323.08, 174.3) * mm, "end": v(-312.92, 174.3) * mm});
            skLineSegment(sketch, "E104.1.0.10", {"start": v(-323.08, 174.3) * mm, "end": v(-323.08, 179.24) * mm});
            skLineSegment(sketch, "E104.direction1", {"start": v(-329.02, 232.32) * mm, "end": v(-329.43, 186.86) * mm, "construction": true});
            skLineSegment(sketch, "E105", {"start": v(-314.19, 186.86) * mm, "end": v(-306.57, 186.86) * mm});
            skSolve(sketch);
        }
        {
            var Q0;
            Q0 = qSketchRegion(id + "F32", true);
            extrude(context, id + "F33", {"entities" : qUnion([Q0]), "operationType" : NewBodyOperationType.REMOVE, "oppositeDirection" : true, "depth" : 2.54 * mm, "offsetDistance" : 25.4 * mm});
        }
    });
